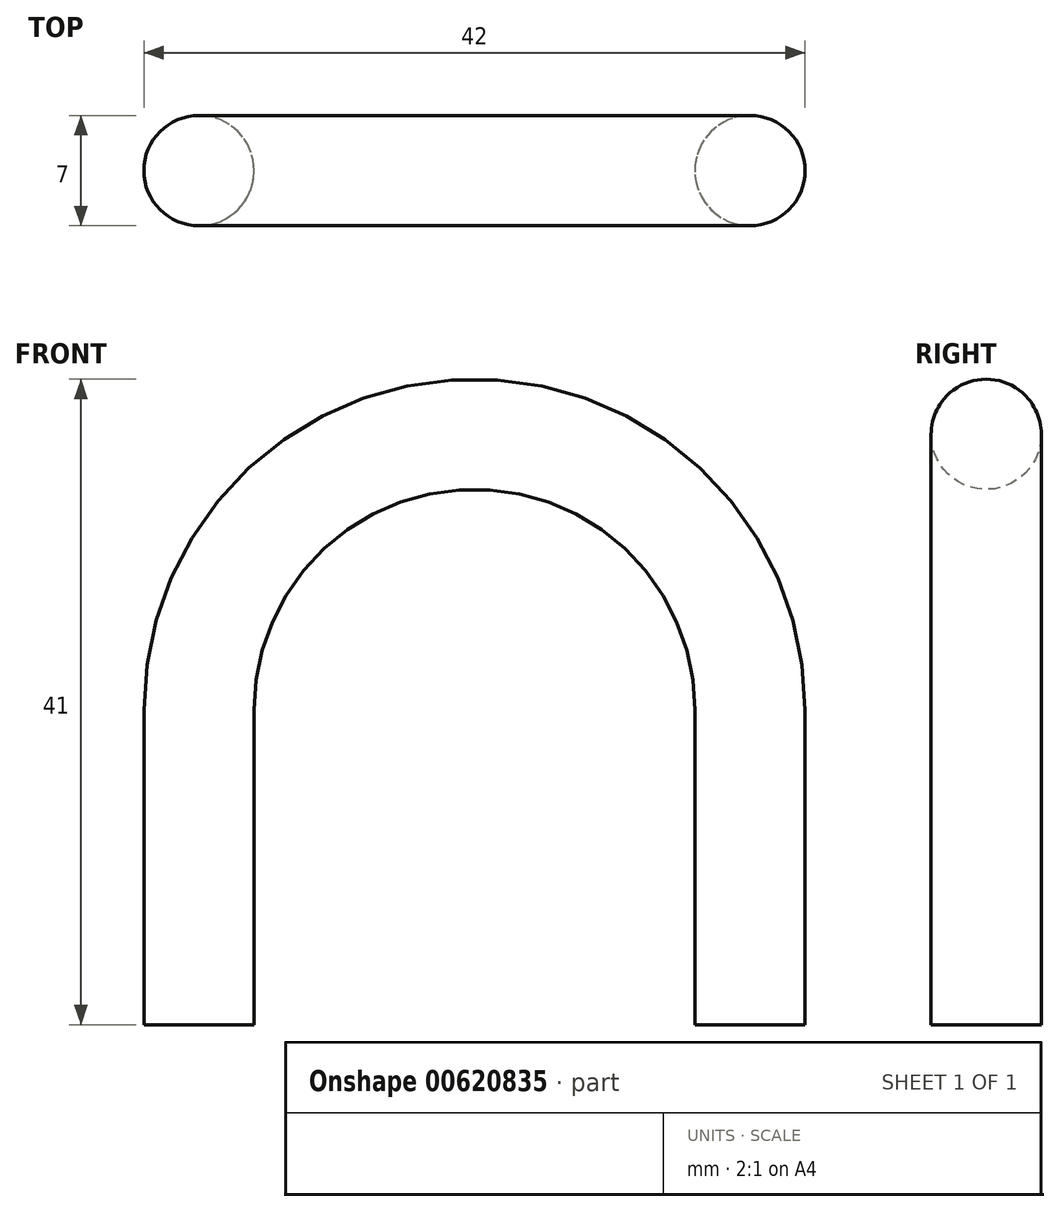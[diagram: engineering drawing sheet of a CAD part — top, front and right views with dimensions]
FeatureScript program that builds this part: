
annotation { "Feature Type Name" : "Feature", "Feature Type Description" : "" }
export const myFeature = defineFeature(function(context is Context, id is Id, definition is map)
    precondition{}
    {
        {
            var Q0;
            Q0=qCreatedBy(makeId("Front.planeOp"),FACE);
            var sketch = newSketch(context, id + "F0", { "sketchPlane" : qUnion([Q0])});
            skLineSegment(sketch, "E0", {"start": v(17.5, 0) * mm, "end": v(17.5, 20) * mm});
            skArc(sketch, "E1", {"start": v(17.5, 20) * mm, "mid": v(0, 37.5) * mm, "end": v(-17.5, 20) * mm});
            skLineSegment(sketch, "E2", {"start": v(-17.5, 20) * mm, "end": v(-17.5, 0) * mm});
            skSolve(sketch);
        }
        {
            var Q0;
            Q0=qCreatedBy(makeId("Top.planeOp"),FACE);
            var sketch = newSketch(context, id + "F1", { "sketchPlane" : qUnion([Q0])});
            skCircle(sketch, "E3", {"center": v(17.5, 0) * mm, "radius": 3.5 * mm});
            skSolve(sketch);
        }
        {
            var Q0;
            Q0=makeQuery(id+"F1.imprint","IMPRINT",FACE,{"disambiguationData":[TD([[makeQuery(id+"F1.imprint","IMPRINT",EDGE,{"derivedFrom":sQuery(id+"F1.wireOp",EDGE,"E3")}),1.0]])]});
            var Q1;
            Q1=qConstructionFilter(qBodyType(qCreatedBy(id+"F0",EDGE),BodyType.WIRE),ConstructionObject.NO);
            sweep(context, id + "F2", {"profiles" : qUnion([Q0]), "path" : qUnion([Q1])});
        }
    });
